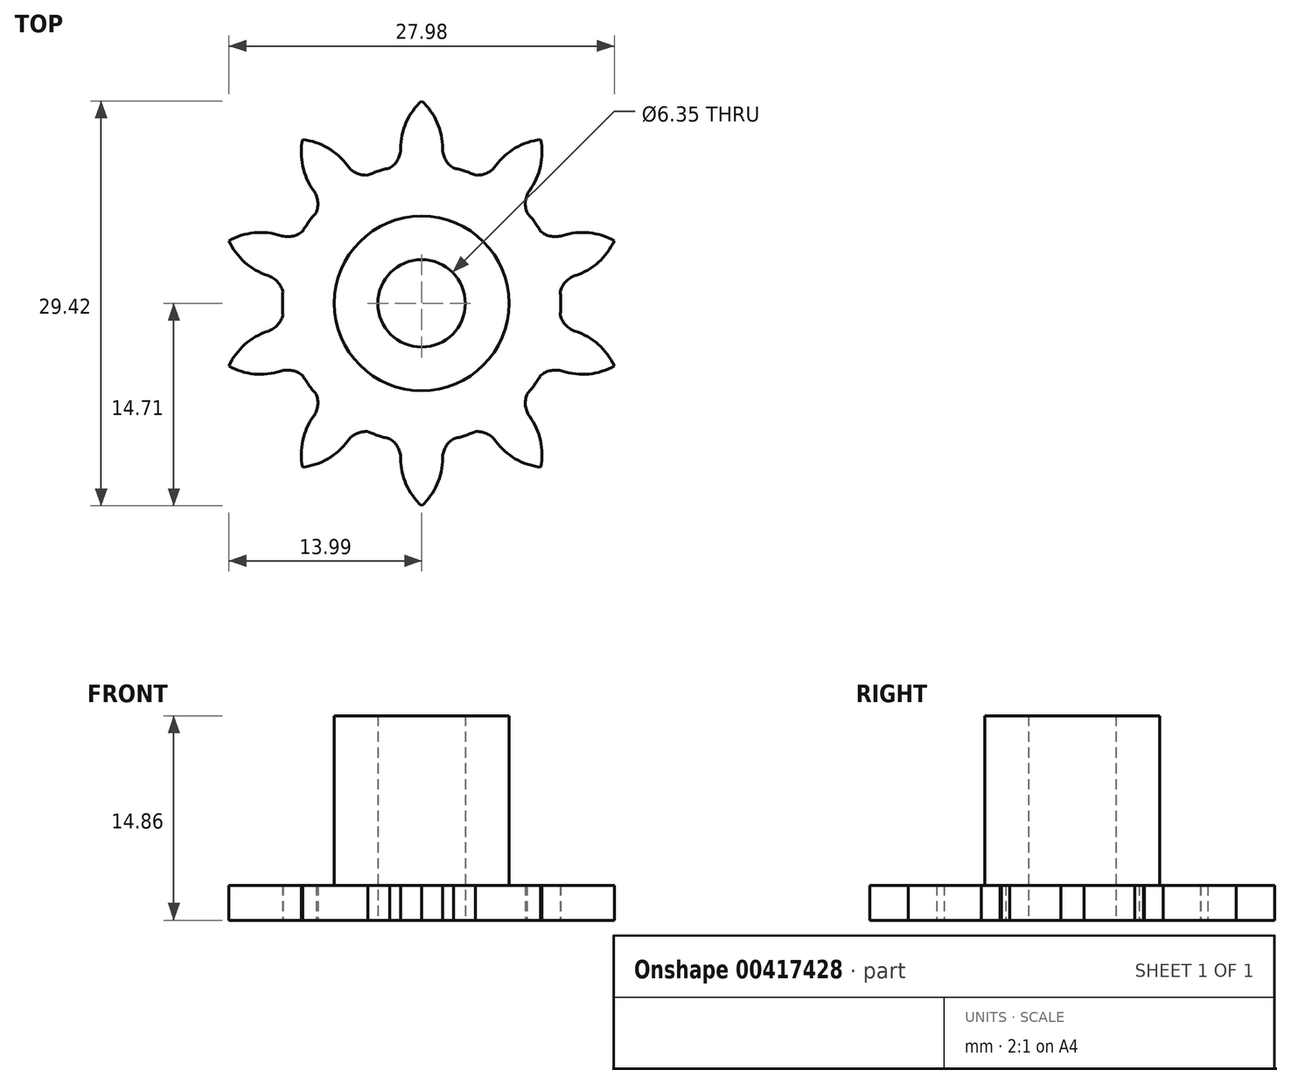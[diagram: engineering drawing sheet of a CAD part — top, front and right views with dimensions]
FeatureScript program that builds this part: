
annotation { "Feature Type Name" : "Feature", "Feature Type Description" : "" }
export const myFeature = defineFeature(function(context is Context, id is Id, definition is map)
    precondition{}
    {
        {
            var Q0;
            Q0=qCreatedBy(makeId("Top.planeOp"),FACE);
            var sketch = newSketch(context, id + "F0", { "sketchPlane" : qUnion([Q0])});
            skCircle(sketch, "E0", {"center": v(0, 0) * mm, "radius": 10.1 * mm});
            skArc(sketch, "E1", {"start": v(-3.18, 9.6) * mm, "mid": v(-2, 10.08) * mm, "end": v(-1.52, 11.25) * mm});
            skArc(sketch, "E2", {"start": v(1.52, 11.25) * mm, "mid": v(2, 10.08) * mm, "end": v(3.18, 9.6) * mm});
            skArc(sketch, "E3", {"start": v(0, 14.71) * mm, "mid": v(-1.13, 13.14) * mm, "end": v(-1.52, 11.25) * mm});
            skArc(sketch, "E4", {"start": v(1.22, 9.6) * mm, "mid": v(1.3, 9.8) * mm, "end": v(1.36, 10.02) * mm});
            skPoint(sketch, "E5", {"position": v(3.18, 9.6) * mm});
            skPoint(sketch, "E6", {"position": v(-3.18, 9.6) * mm});
            skLineSegment(sketch, "E7", {"start": v(-3.18, 9.6) * mm, "end": v(3.18, 9.6) * mm});
            skArc(sketch, "E8.trimOffspring", {"start": v(1.52, 11.25) * mm, "mid": v(1.13, 13.14) * mm, "end": v(0, 14.71) * mm});
            skArc(sketch, "E9.trimOffspring", {"start": v(-1.36, 10.02) * mm, "mid": v(-1.3, 9.8) * mm, "end": v(-1.22, 9.6) * mm});
            skArc(sketch, "E10.1.0", {"start": v(-5.38, 10) * mm, "mid": v(-6.81, 11.3) * mm, "end": v(-8.65, 11.9) * mm});
            skLineSegment(sketch, "E10.1.1", {"start": v(-8.2, 5.9) * mm, "end": v(-3.07, 9.63) * mm});
            skArc(sketch, "E10.1.2", {"start": v(-8.2, 5.9) * mm, "mid": v(-7.55, 6.98) * mm, "end": v(-7.84, 8.2) * mm});
            skArc(sketch, "E10.1.3", {"start": v(-8.65, 11.9) * mm, "mid": v(-8.63, 9.97) * mm, "end": v(-7.84, 8.2) * mm});
            skPoint(sketch, "E10.1.4", {"position": v(-3.07, 9.63) * mm});
            skArc(sketch, "E10.1.5", {"start": v(-5.38, 10) * mm, "mid": v(-4.3, 9.34) * mm, "end": v(-3.07, 9.63) * mm});
            skPoint(sketch, "E10.1.6", {"position": v(-8.2, 5.9) * mm});
            skArc(sketch, "E10.1.7", {"start": v(-6.99, 7.3) * mm, "mid": v(-6.81, 7.17) * mm, "end": v(-6.63, 7.04) * mm});
            skArc(sketch, "E10.1.8", {"start": v(-4.65, 8.48) * mm, "mid": v(-4.71, 8.7) * mm, "end": v(-4.79, 8.9) * mm});
            skArc(sketch, "E10.2.0", {"start": v(-10.23, 4.93) * mm, "mid": v(-12.15, 5.13) * mm, "end": v(-14, 4.55) * mm});
            skLineSegment(sketch, "E10.2.1", {"start": v(-10.1, -0.05) * mm, "end": v(-8.15, 5.99) * mm});
            skArc(sketch, "E10.2.2", {"start": v(-10.1, -0.05) * mm, "mid": v(-10.2, 1.2) * mm, "end": v(-11.17, 2.03) * mm});
            skArc(sketch, "E10.2.3", {"start": v(-14, 4.55) * mm, "mid": v(-12.84, 2.99) * mm, "end": v(-11.17, 2.03) * mm});
            skPoint(sketch, "E10.2.4", {"position": v(-8.15, 5.99) * mm});
            skArc(sketch, "E10.2.5", {"start": v(-10.23, 4.93) * mm, "mid": v(-8.97, 5.02) * mm, "end": v(-8.15, 5.99) * mm});
            skPoint(sketch, "E10.2.6", {"position": v(-10.1, -0.05) * mm});
            skArc(sketch, "E10.2.7", {"start": v(-9.95, 1.8) * mm, "mid": v(-9.73, 1.8) * mm, "end": v(-9.5, 1.8) * mm});
            skArc(sketch, "E10.2.8", {"start": v(-8.75, 4.13) * mm, "mid": v(-8.92, 4.26) * mm, "end": v(-9.1, 4.39) * mm});
            skArc(sketch, "E10.3.0", {"start": v(-11.17, -2.03) * mm, "mid": v(-12.84, -2.99) * mm, "end": v(-14, -4.55) * mm});
            skLineSegment(sketch, "E10.3.1", {"start": v(-8.15, -5.99) * mm, "end": v(-10.1, 0.05) * mm});
            skArc(sketch, "E10.3.2", {"start": v(-8.15, -5.99) * mm, "mid": v(-8.97, -5.02) * mm, "end": v(-10.23, -4.93) * mm});
            skArc(sketch, "E10.3.3", {"start": v(-14, -4.55) * mm, "mid": v(-12.15, -5.13) * mm, "end": v(-10.23, -4.93) * mm});
            skPoint(sketch, "E10.3.4", {"position": v(-10.1, 0.05) * mm});
            skArc(sketch, "E10.3.5", {"start": v(-11.17, -2.03) * mm, "mid": v(-10.2, -1.2) * mm, "end": v(-10.1, 0.05) * mm});
            skPoint(sketch, "E10.3.6", {"position": v(-8.15, -5.99) * mm});
            skArc(sketch, "E10.3.7", {"start": v(-9.1, -4.39) * mm, "mid": v(-8.92, -4.26) * mm, "end": v(-8.75, -4.13) * mm});
            skArc(sketch, "E10.3.8", {"start": v(-9.5, -1.8) * mm, "mid": v(-9.73, -1.8) * mm, "end": v(-9.95, -1.8) * mm});
            skArc(sketch, "E10.4.0", {"start": v(-7.84, -8.2) * mm, "mid": v(-8.63, -9.97) * mm, "end": v(-8.65, -11.9) * mm});
            skLineSegment(sketch, "E10.4.1", {"start": v(-3.07, -9.63) * mm, "end": v(-8.2, -5.9) * mm});
            skArc(sketch, "E10.4.2", {"start": v(-3.07, -9.63) * mm, "mid": v(-4.3, -9.34) * mm, "end": v(-5.38, -10) * mm});
            skArc(sketch, "E10.4.3", {"start": v(-8.65, -11.9) * mm, "mid": v(-6.81, -11.3) * mm, "end": v(-5.38, -10) * mm});
            skPoint(sketch, "E10.4.4", {"position": v(-8.2, -5.9) * mm});
            skArc(sketch, "E10.4.5", {"start": v(-7.84, -8.2) * mm, "mid": v(-7.55, -6.98) * mm, "end": v(-8.2, -5.9) * mm});
            skPoint(sketch, "E10.4.6", {"position": v(-3.07, -9.63) * mm});
            skArc(sketch, "E10.4.7", {"start": v(-4.79, -8.9) * mm, "mid": v(-4.71, -8.7) * mm, "end": v(-4.65, -8.48) * mm});
            skArc(sketch, "E10.4.8", {"start": v(-6.63, -7.04) * mm, "mid": v(-6.81, -7.17) * mm, "end": v(-6.99, -7.3) * mm});
            skArc(sketch, "E10.5.0", {"start": v(-1.52, -11.25) * mm, "mid": v(-1.13, -13.14) * mm, "end": v(0, -14.71) * mm});
            skLineSegment(sketch, "E10.5.1", {"start": v(3.17, -9.6) * mm, "end": v(-3.18, -9.6) * mm});
            skArc(sketch, "E10.5.2", {"start": v(3.17, -9.6) * mm, "mid": v(2, -10.08) * mm, "end": v(1.52, -11.25) * mm});
            skArc(sketch, "E10.5.3", {"start": v(0, -14.71) * mm, "mid": v(1.13, -13.14) * mm, "end": v(1.52, -11.25) * mm});
            skPoint(sketch, "E10.5.4", {"position": v(-3.18, -9.6) * mm});
            skArc(sketch, "E10.5.5", {"start": v(-1.52, -11.25) * mm, "mid": v(-2, -10.08) * mm, "end": v(-3.18, -9.6) * mm});
            skPoint(sketch, "E10.5.6", {"position": v(3.17, -9.6) * mm});
            skArc(sketch, "E10.5.7", {"start": v(1.36, -10.02) * mm, "mid": v(1.3, -9.8) * mm, "end": v(1.22, -9.6) * mm});
            skArc(sketch, "E10.5.8", {"start": v(-1.22, -9.6) * mm, "mid": v(-1.3, -9.8) * mm, "end": v(-1.36, -10.02) * mm});
            skArc(sketch, "E10.6.0", {"start": v(5.38, -10) * mm, "mid": v(6.81, -11.3) * mm, "end": v(8.65, -11.9) * mm});
            skLineSegment(sketch, "E10.6.1", {"start": v(8.2, -5.9) * mm, "end": v(3.07, -9.63) * mm});
            skArc(sketch, "E10.6.2", {"start": v(8.2, -5.9) * mm, "mid": v(7.55, -6.98) * mm, "end": v(7.84, -8.2) * mm});
            skArc(sketch, "E10.6.3", {"start": v(8.65, -11.9) * mm, "mid": v(8.63, -9.97) * mm, "end": v(7.84, -8.2) * mm});
            skPoint(sketch, "E10.6.4", {"position": v(3.07, -9.63) * mm});
            skArc(sketch, "E10.6.5", {"start": v(5.38, -10) * mm, "mid": v(4.3, -9.34) * mm, "end": v(3.07, -9.63) * mm});
            skPoint(sketch, "E10.6.6", {"position": v(8.2, -5.9) * mm});
            skArc(sketch, "E10.6.7", {"start": v(6.99, -7.3) * mm, "mid": v(6.81, -7.17) * mm, "end": v(6.63, -7.04) * mm});
            skArc(sketch, "E10.6.8", {"start": v(4.65, -8.48) * mm, "mid": v(4.71, -8.7) * mm, "end": v(4.79, -8.9) * mm});
            skArc(sketch, "E10.7.0", {"start": v(10.23, -4.93) * mm, "mid": v(12.15, -5.13) * mm, "end": v(14, -4.55) * mm});
            skLineSegment(sketch, "E10.7.1", {"start": v(10.1, 0.05) * mm, "end": v(8.15, -5.99) * mm});
            skArc(sketch, "E10.7.2", {"start": v(10.1, 0.05) * mm, "mid": v(10.2, -1.2) * mm, "end": v(11.17, -2.03) * mm});
            skArc(sketch, "E10.7.3", {"start": v(14, -4.55) * mm, "mid": v(12.84, -2.99) * mm, "end": v(11.17, -2.03) * mm});
            skPoint(sketch, "E10.7.4", {"position": v(8.15, -5.99) * mm});
            skArc(sketch, "E10.7.5", {"start": v(10.23, -4.93) * mm, "mid": v(8.97, -5.02) * mm, "end": v(8.15, -5.99) * mm});
            skPoint(sketch, "E10.7.6", {"position": v(10.1, 0.05) * mm});
            skArc(sketch, "E10.7.7", {"start": v(9.95, -1.8) * mm, "mid": v(9.73, -1.8) * mm, "end": v(9.5, -1.8) * mm});
            skArc(sketch, "E10.7.8", {"start": v(8.75, -4.13) * mm, "mid": v(8.92, -4.26) * mm, "end": v(9.1, -4.39) * mm});
            skArc(sketch, "E10.8.0", {"start": v(11.17, 2.03) * mm, "mid": v(12.84, 2.99) * mm, "end": v(14, 4.55) * mm});
            skLineSegment(sketch, "E10.8.1", {"start": v(8.15, 5.99) * mm, "end": v(10.1, -0.05) * mm});
            skArc(sketch, "E10.8.2", {"start": v(8.15, 5.99) * mm, "mid": v(8.97, 5.02) * mm, "end": v(10.23, 4.93) * mm});
            skArc(sketch, "E10.8.3", {"start": v(14, 4.55) * mm, "mid": v(12.15, 5.13) * mm, "end": v(10.23, 4.93) * mm});
            skPoint(sketch, "E10.8.4", {"position": v(10.1, -0.05) * mm});
            skArc(sketch, "E10.8.5", {"start": v(11.17, 2.03) * mm, "mid": v(10.2, 1.2) * mm, "end": v(10.1, -0.05) * mm});
            skPoint(sketch, "E10.8.6", {"position": v(8.15, 5.99) * mm});
            skArc(sketch, "E10.8.7", {"start": v(9.1, 4.39) * mm, "mid": v(8.92, 4.26) * mm, "end": v(8.75, 4.13) * mm});
            skArc(sketch, "E10.8.8", {"start": v(9.5, 1.8) * mm, "mid": v(9.73, 1.8) * mm, "end": v(9.95, 1.8) * mm});
            skArc(sketch, "E10.9.0", {"start": v(7.84, 8.2) * mm, "mid": v(8.63, 9.97) * mm, "end": v(8.65, 11.9) * mm});
            skLineSegment(sketch, "E10.9.1", {"start": v(3.07, 9.63) * mm, "end": v(8.2, 5.9) * mm});
            skArc(sketch, "E10.9.2", {"start": v(3.07, 9.63) * mm, "mid": v(4.3, 9.34) * mm, "end": v(5.38, 10) * mm});
            skArc(sketch, "E10.9.3", {"start": v(8.65, 11.9) * mm, "mid": v(6.81, 11.3) * mm, "end": v(5.38, 10) * mm});
            skPoint(sketch, "E10.9.4", {"position": v(8.2, 5.9) * mm});
            skArc(sketch, "E10.9.5", {"start": v(7.84, 8.2) * mm, "mid": v(7.55, 6.98) * mm, "end": v(8.2, 5.9) * mm});
            skPoint(sketch, "E10.9.6", {"position": v(3.07, 9.63) * mm});
            skArc(sketch, "E10.9.7", {"start": v(4.79, 8.9) * mm, "mid": v(4.71, 8.7) * mm, "end": v(4.65, 8.48) * mm});
            skArc(sketch, "E10.9.8", {"start": v(6.63, 7.04) * mm, "mid": v(6.81, 7.17) * mm, "end": v(6.99, 7.3) * mm});
            skCircle(sketch, "E11", {"center": v(0, 0) * mm, "radius": 6.35 * mm});
            skCircle(sketch, "E12", {"center": v(0, 0) * mm, "radius": 3.18 * mm});
            skSolve(sketch);
        }
        {
            var Q0;
            {var subQ5=sQuery(id+"F0.wireOp",EDGE,"E10.2.8");Q0=makeQuery(id+"F0.imprint","IMPRINT",FACE,{"disambiguationData":[TD([[makeQuery(id+"F0.imprint","IMPRINT",EDGE,{"derivedFrom":subQ5}),-1.0]])]});}
            var Q1;
            {var subQ0=sQuery(id+"F0.wireOp",EDGE,"E10.3.7");Q1=makeQuery(id+"F0.imprint","IMPRINT",FACE,{"disambiguationData":[TD([[makeQuery(id+"F0.imprint","IMPRINT",EDGE,{"derivedFrom":subQ0}),-1.0]])]});}
            var Q2;
            {var subQ0=sQuery(id+"F0.wireOp",EDGE,"E10.2.7");Q2=makeQuery(id+"F0.imprint","IMPRINT",FACE,{"disambiguationData":[TD([[makeQuery(id+"F0.imprint","IMPRINT",EDGE,{"derivedFrom":subQ0}),-1.0]])]});}
            var Q3;
            {var subQ0=sQuery(id+"F0.wireOp",EDGE,"E10.8.7");Q3=makeQuery(id+"F0.imprint","IMPRINT",FACE,{"disambiguationData":[TD([[makeQuery(id+"F0.imprint","IMPRINT",EDGE,{"derivedFrom":subQ0}),1.0]])]});}
            var Q4;
            {var subQ5=sQuery(id+"F0.wireOp",EDGE,"E10.4.8");Q4=makeQuery(id+"F0.imprint","IMPRINT",FACE,{"disambiguationData":[TD([[makeQuery(id+"F0.imprint","IMPRINT",EDGE,{"derivedFrom":subQ5}),-1.0]])]});}
            var Q5;
            {var subQ0=sQuery(id+"F0.wireOp",EDGE,"E10.3.8");Q5=makeQuery(id+"F0.imprint","IMPRINT",FACE,{"disambiguationData":[TD([[makeQuery(id+"F0.imprint","IMPRINT",EDGE,{"derivedFrom":subQ0}),-1.0]])]});}
            var Q6;
            {var subQ0=sQuery(id+"F0.wireOp",EDGE,"E4");Q6=makeQuery(id+"F0.imprint","IMPRINT",FACE,{"disambiguationData":[TD([[makeQuery(id+"F0.imprint","IMPRINT",EDGE,{"derivedFrom":subQ0}),1.0]])]});}
            var Q7;
            {var subQ4=sQuery(id+"F0.wireOp",EDGE,"E10.8.0");Q7=makeQuery(id+"F0.imprint","IMPRINT",FACE,{"disambiguationData":[TD([[makeQuery(id+"F0.imprint","IMPRINT",EDGE,{"derivedFrom":subQ4}),1.0]])]});}
            var Q8;
            {var subQ5=sQuery(id+"F0.wireOp",EDGE,"E10.5.8");Q8=makeQuery(id+"F0.imprint","IMPRINT",FACE,{"disambiguationData":[TD([[makeQuery(id+"F0.imprint","IMPRINT",EDGE,{"derivedFrom":subQ5}),-1.0]])]});}
            var Q9;
            {var subQ0=sQuery(id+"F0.wireOp",EDGE,"E10.1.7");Q9=makeQuery(id+"F0.imprint","IMPRINT",FACE,{"disambiguationData":[TD([[makeQuery(id+"F0.imprint","IMPRINT",EDGE,{"derivedFrom":subQ0}),1.0]])]});}
            var Q10;
            {var subQ0=sQuery(id+"F0.wireOp",EDGE,"E10.9.0");Q10=makeQuery(id+"F0.imprint","IMPRINT",FACE,{"disambiguationData":[TD([[makeQuery(id+"F0.imprint","IMPRINT",EDGE,{"derivedFrom":subQ0}),1.0]])]});}
            var Q11;
            {var subQ0=sQuery(id+"F0.wireOp",EDGE,"E10.5.7");Q11=makeQuery(id+"F0.imprint","IMPRINT",FACE,{"disambiguationData":[TD([[makeQuery(id+"F0.imprint","IMPRINT",EDGE,{"derivedFrom":subQ0}),-1.0]])]});}
            var Q12;
            {var subQ0=sQuery(id+"F0.wireOp",EDGE,"E10.2.7");Q12=makeQuery(id+"F0.imprint","IMPRINT",FACE,{"disambiguationData":[TD([[makeQuery(id+"F0.imprint","IMPRINT",EDGE,{"derivedFrom":subQ0}),1.0]])]});}
            var Q13;
            {var subQ0=sQuery(id+"F0.wireOp",EDGE,"E10.8.8");Q13=makeQuery(id+"F0.imprint","IMPRINT",FACE,{"disambiguationData":[TD([[makeQuery(id+"F0.imprint","IMPRINT",EDGE,{"derivedFrom":subQ0}),-1.0]])]});}
            var Q14;
            {var subQ5=sQuery(id+"F0.wireOp",EDGE,"E3");Q14=makeQuery(id+"F0.imprint","IMPRINT",FACE,{"disambiguationData":[TD([[makeQuery(id+"F0.imprint","IMPRINT",EDGE,{"derivedFrom":subQ5}),1.0]])]});}
            var Q15;
            {var subQ7=sQuery(id+"F0.wireOp",EDGE,"E10.6.8");Q15=makeQuery(id+"F0.imprint","IMPRINT",FACE,{"disambiguationData":[TD([[makeQuery(id+"F0.imprint","IMPRINT",EDGE,{"derivedFrom":subQ7}),-1.0]])]});}
            var Q16;
            {var subQ0=sQuery(id+"F0.wireOp",EDGE,"E10.8.7");Q16=makeQuery(id+"F0.imprint","IMPRINT",FACE,{"disambiguationData":[TD([[makeQuery(id+"F0.imprint","IMPRINT",EDGE,{"derivedFrom":subQ0}),-1.0]])]});}
            var Q17;
            {var subQ0=sQuery(id+"F0.wireOp",EDGE,"E10.3.7");Q17=makeQuery(id+"F0.imprint","IMPRINT",FACE,{"disambiguationData":[TD([[makeQuery(id+"F0.imprint","IMPRINT",EDGE,{"derivedFrom":subQ0}),1.0]])]});}
            var Q18;
            {var subQ5=sQuery(id+"F0.wireOp",EDGE,"E10.1.0");Q18=makeQuery(id+"F0.imprint","IMPRINT",FACE,{"disambiguationData":[TD([[makeQuery(id+"F0.imprint","IMPRINT",EDGE,{"derivedFrom":subQ5}),1.0]])]});}
            var Q19;
            {var subQ5=sQuery(id+"F0.wireOp",EDGE,"E10.6.7");Q19=makeQuery(id+"F0.imprint","IMPRINT",FACE,{"disambiguationData":[TD([[makeQuery(id+"F0.imprint","IMPRINT",EDGE,{"derivedFrom":subQ5}),-1.0]])]});}
            var Q20;
            {var subQ5=sQuery(id+"F0.wireOp",EDGE,"E10.9.8");Q20=makeQuery(id+"F0.imprint","IMPRINT",FACE,{"disambiguationData":[TD([[makeQuery(id+"F0.imprint","IMPRINT",EDGE,{"derivedFrom":subQ5}),-1.0]])]});}
            var Q21;
            {var subQ0=sQuery(id+"F0.wireOp",EDGE,"E10.4.7");Q21=makeQuery(id+"F0.imprint","IMPRINT",FACE,{"disambiguationData":[TD([[makeQuery(id+"F0.imprint","IMPRINT",EDGE,{"derivedFrom":subQ0}),1.0]])]});}
            var Q22;
            {var subQ0=sQuery(id+"F0.wireOp",EDGE,"E10.2.0");Q22=makeQuery(id+"F0.imprint","IMPRINT",FACE,{"disambiguationData":[TD([[makeQuery(id+"F0.imprint","IMPRINT",EDGE,{"derivedFrom":subQ0}),1.0]])]});}
            var Q23;
            {var subQ5=sQuery(id+"F0.wireOp",EDGE,"E10.7.8");Q23=makeQuery(id+"F0.imprint","IMPRINT",FACE,{"disambiguationData":[TD([[makeQuery(id+"F0.imprint","IMPRINT",EDGE,{"derivedFrom":subQ5}),-1.0]])]});}
            var Q24;
            {var subQ7=sQuery(id+"F0.wireOp",EDGE,"E10.9.7");Q24=makeQuery(id+"F0.imprint","IMPRINT",FACE,{"disambiguationData":[TD([[makeQuery(id+"F0.imprint","IMPRINT",EDGE,{"derivedFrom":subQ7}),-1.0]])]});}
            var Q25;
            {var subQ0=sQuery(id+"F0.wireOp",EDGE,"E10.5.7");Q25=makeQuery(id+"F0.imprint","IMPRINT",FACE,{"disambiguationData":[TD([[makeQuery(id+"F0.imprint","IMPRINT",EDGE,{"derivedFrom":subQ0}),1.0]])]});}
            var Q26;
            {var subQ4=sQuery(id+"F0.wireOp",EDGE,"E10.3.0");Q26=makeQuery(id+"F0.imprint","IMPRINT",FACE,{"disambiguationData":[TD([[makeQuery(id+"F0.imprint","IMPRINT",EDGE,{"derivedFrom":subQ4}),1.0]])]});}
            var Q27;
            {var subQ0=sQuery(id+"F0.wireOp",EDGE,"E10.7.7");Q27=makeQuery(id+"F0.imprint","IMPRINT",FACE,{"disambiguationData":[TD([[makeQuery(id+"F0.imprint","IMPRINT",EDGE,{"derivedFrom":subQ0}),-1.0]])]});}
            var Q28;
            Q28=makeQuery(id+"F0.imprint","IMPRINT",FACE,{"disambiguationData":[TD([[makeQuery(id+"F0.imprint","IMPRINT",EDGE,{"derivedFrom":sQuery(id+"F0.wireOp",EDGE,"E11")}),-1.0]])]});
            var Q29;
            {var subQ1=sQuery(id+"F0.wireOp",EDGE,"E4");Q29=makeQuery(id+"F0.imprint","IMPRINT",FACE,{"disambiguationData":[TD([[makeQuery(id+"F0.imprint","IMPRINT",EDGE,{"derivedFrom":subQ1}),-1.0]])]});}
            var Q30;
            {var subQ0=sQuery(id+"F0.wireOp",EDGE,"E10.6.7");Q30=makeQuery(id+"F0.imprint","IMPRINT",FACE,{"disambiguationData":[TD([[makeQuery(id+"F0.imprint","IMPRINT",EDGE,{"derivedFrom":subQ0}),1.0]])]});}
            var Q31;
            {var subQ0=sQuery(id+"F0.wireOp",EDGE,"E10.4.0");Q31=makeQuery(id+"F0.imprint","IMPRINT",FACE,{"disambiguationData":[TD([[makeQuery(id+"F0.imprint","IMPRINT",EDGE,{"derivedFrom":subQ0}),1.0]])]});}
            var Q32;
            {var subQ0=sQuery(id+"F0.wireOp",EDGE,"E10.5.0");Q32=makeQuery(id+"F0.imprint","IMPRINT",FACE,{"disambiguationData":[TD([[makeQuery(id+"F0.imprint","IMPRINT",EDGE,{"derivedFrom":subQ0}),1.0]])]});}
            var Q33;
            {var subQ0=sQuery(id+"F0.wireOp",EDGE,"E9.trimOffspring");Q33=makeQuery(id+"F0.imprint","IMPRINT",FACE,{"disambiguationData":[TD([[makeQuery(id+"F0.imprint","IMPRINT",EDGE,{"derivedFrom":subQ0}),-1.0]])]});}
            var Q34;
            {var subQ0=sQuery(id+"F0.wireOp",EDGE,"E10.7.7");Q34=makeQuery(id+"F0.imprint","IMPRINT",FACE,{"disambiguationData":[TD([[makeQuery(id+"F0.imprint","IMPRINT",EDGE,{"derivedFrom":subQ0}),1.0]])]});}
            var Q35;
            {var subQ5=sQuery(id+"F0.wireOp",EDGE,"E10.6.0");Q35=makeQuery(id+"F0.imprint","IMPRINT",FACE,{"disambiguationData":[TD([[makeQuery(id+"F0.imprint","IMPRINT",EDGE,{"derivedFrom":subQ5}),1.0]])]});}
            var Q36;
            {var subQ7=sQuery(id+"F0.wireOp",EDGE,"E10.1.8");Q36=makeQuery(id+"F0.imprint","IMPRINT",FACE,{"disambiguationData":[TD([[makeQuery(id+"F0.imprint","IMPRINT",EDGE,{"derivedFrom":subQ7}),-1.0]])]});}
            var Q37;
            {var subQ0=sQuery(id+"F0.wireOp",EDGE,"E10.7.0");Q37=makeQuery(id+"F0.imprint","IMPRINT",FACE,{"disambiguationData":[TD([[makeQuery(id+"F0.imprint","IMPRINT",EDGE,{"derivedFrom":subQ0}),1.0]])]});}
            var Q38;
            {var subQ0=sQuery(id+"F0.wireOp",EDGE,"E10.4.7");Q38=makeQuery(id+"F0.imprint","IMPRINT",FACE,{"disambiguationData":[TD([[makeQuery(id+"F0.imprint","IMPRINT",EDGE,{"derivedFrom":subQ0}),-1.0]])]});}
            var Q39;
            {var subQ0=sQuery(id+"F0.wireOp",EDGE,"E10.9.7");Q39=makeQuery(id+"F0.imprint","IMPRINT",FACE,{"disambiguationData":[TD([[makeQuery(id+"F0.imprint","IMPRINT",EDGE,{"derivedFrom":subQ0}),1.0]])]});}
            var Q40;
            {var subQ5=sQuery(id+"F0.wireOp",EDGE,"E10.1.7");Q40=makeQuery(id+"F0.imprint","IMPRINT",FACE,{"disambiguationData":[TD([[makeQuery(id+"F0.imprint","IMPRINT",EDGE,{"derivedFrom":subQ5}),-1.0]])]});}
            var Q41;
            {var subQ1=sQuery(id+"F0.wireOp",EDGE,"E0");var subQ3=sQuery(id+"F0.wireOp",EDGE,"E10.6.2");var subQ4=makeQuery(id+"F0.imprint","INTERSECT",VERTEX,{"derivedFrom":[subQ1,subQ3]});Q41=makeQuery(id+"F0.imprint","IMPRINT",FACE,{"disambiguationData":[TD([[makeQuery(id+"F0.imprint","IMPRINT",EDGE,{"disambiguationData":[TD([[subQ4,1.0]])],"derivedFrom":subQ3}),1.0]])]});}
            var Q42;
            {var subQ1=sQuery(id+"F0.wireOp",EDGE,"E0");var subQ3=sQuery(id+"F0.wireOp",EDGE,"E10.7.2");var subQ4=makeQuery(id+"F0.imprint","INTERSECT",VERTEX,{"derivedFrom":[subQ1,subQ3]});Q42=makeQuery(id+"F0.imprint","IMPRINT",FACE,{"disambiguationData":[TD([[makeQuery(id+"F0.imprint","IMPRINT",EDGE,{"disambiguationData":[TD([[subQ4,1.0]])],"derivedFrom":subQ3}),1.0]])]});}
            var Q43;
            {var subQ1=sQuery(id+"F0.wireOp",EDGE,"E0");var subQ3=sQuery(id+"F0.wireOp",EDGE,"E10.7.5");var subQ4=makeQuery(id+"F0.imprint","INTERSECT",VERTEX,{"derivedFrom":[subQ1,subQ3]});Q43=makeQuery(id+"F0.imprint","IMPRINT",FACE,{"disambiguationData":[TD([[makeQuery(id+"F0.imprint","IMPRINT",EDGE,{"disambiguationData":[TD([[subQ4,-1.0]])],"derivedFrom":subQ3}),1.0]])]});}
            var Q44;
            {var subQ1=sQuery(id+"F0.wireOp",EDGE,"E0");var subQ3=sQuery(id+"F0.wireOp",EDGE,"E10.3.5");var subQ4=makeQuery(id+"F0.imprint","INTERSECT",VERTEX,{"derivedFrom":[subQ1,subQ3]});Q44=makeQuery(id+"F0.imprint","IMPRINT",FACE,{"disambiguationData":[TD([[makeQuery(id+"F0.imprint","IMPRINT",EDGE,{"disambiguationData":[TD([[subQ4,-1.0]])],"derivedFrom":subQ3}),1.0]])]});}
            var Q45;
            {var subQ1=sQuery(id+"F0.wireOp",EDGE,"E0");var subQ3=sQuery(id+"F0.wireOp",EDGE,"E10.3.2");var subQ4=makeQuery(id+"F0.imprint","INTERSECT",VERTEX,{"derivedFrom":[subQ1,subQ3]});Q45=makeQuery(id+"F0.imprint","IMPRINT",FACE,{"disambiguationData":[TD([[makeQuery(id+"F0.imprint","IMPRINT",EDGE,{"disambiguationData":[TD([[subQ4,1.0]])],"derivedFrom":subQ3}),1.0]])]});}
            var Q46;
            {var subQ1=sQuery(id+"F0.wireOp",EDGE,"E0");var subQ3=sQuery(id+"F0.wireOp",EDGE,"E10.4.5");var subQ4=makeQuery(id+"F0.imprint","INTERSECT",VERTEX,{"derivedFrom":[subQ1,subQ3]});Q46=makeQuery(id+"F0.imprint","IMPRINT",FACE,{"disambiguationData":[TD([[makeQuery(id+"F0.imprint","IMPRINT",EDGE,{"disambiguationData":[TD([[subQ4,-1.0]])],"derivedFrom":subQ3}),1.0]])]});}
            var Q47;
            {var subQ1=sQuery(id+"F0.wireOp",EDGE,"E0");var subQ3=sQuery(id+"F0.wireOp",EDGE,"E10.4.2");var subQ4=makeQuery(id+"F0.imprint","INTERSECT",VERTEX,{"derivedFrom":[subQ1,subQ3]});Q47=makeQuery(id+"F0.imprint","IMPRINT",FACE,{"disambiguationData":[TD([[makeQuery(id+"F0.imprint","IMPRINT",EDGE,{"disambiguationData":[TD([[subQ4,1.0]])],"derivedFrom":subQ3}),1.0]])]});}
            var Q48;
            {var subQ1=sQuery(id+"F0.wireOp",EDGE,"E0");var subQ3=sQuery(id+"F0.wireOp",EDGE,"E10.5.5");var subQ4=makeQuery(id+"F0.imprint","INTERSECT",VERTEX,{"derivedFrom":[subQ1,subQ3]});Q48=makeQuery(id+"F0.imprint","IMPRINT",FACE,{"disambiguationData":[TD([[makeQuery(id+"F0.imprint","IMPRINT",EDGE,{"disambiguationData":[TD([[subQ4,-1.0]])],"derivedFrom":subQ3}),1.0]])]});}
            var Q49;
            {var subQ1=sQuery(id+"F0.wireOp",EDGE,"E0");var subQ3=sQuery(id+"F0.wireOp",EDGE,"E10.2.5");var subQ4=makeQuery(id+"F0.imprint","INTERSECT",VERTEX,{"derivedFrom":[subQ1,subQ3]});Q49=makeQuery(id+"F0.imprint","IMPRINT",FACE,{"disambiguationData":[TD([[makeQuery(id+"F0.imprint","IMPRINT",EDGE,{"disambiguationData":[TD([[subQ4,-1.0]])],"derivedFrom":subQ3}),1.0]])]});}
            var Q50;
            {var subQ1=sQuery(id+"F0.wireOp",EDGE,"E0");var subQ3=sQuery(id+"F0.wireOp",EDGE,"E10.2.2");var subQ4=makeQuery(id+"F0.imprint","INTERSECT",VERTEX,{"derivedFrom":[subQ1,subQ3]});Q50=makeQuery(id+"F0.imprint","IMPRINT",FACE,{"disambiguationData":[TD([[makeQuery(id+"F0.imprint","IMPRINT",EDGE,{"disambiguationData":[TD([[subQ4,1.0]])],"derivedFrom":subQ3}),1.0]])]});}
            var Q51;
            {var subQ1=sQuery(id+"F0.wireOp",EDGE,"E0");var subQ3=sQuery(id+"F0.wireOp",EDGE,"E10.8.5");var subQ4=makeQuery(id+"F0.imprint","INTERSECT",VERTEX,{"derivedFrom":[subQ1,subQ3]});Q51=makeQuery(id+"F0.imprint","IMPRINT",FACE,{"disambiguationData":[TD([[makeQuery(id+"F0.imprint","IMPRINT",EDGE,{"disambiguationData":[TD([[subQ4,-1.0]])],"derivedFrom":subQ3}),1.0]])]});}
            var Q52;
            {var subQ1=sQuery(id+"F0.wireOp",EDGE,"E0");var subQ3=sQuery(id+"F0.wireOp",EDGE,"E10.8.2");var subQ4=makeQuery(id+"F0.imprint","INTERSECT",VERTEX,{"derivedFrom":[subQ1,subQ3]});Q52=makeQuery(id+"F0.imprint","IMPRINT",FACE,{"disambiguationData":[TD([[makeQuery(id+"F0.imprint","IMPRINT",EDGE,{"disambiguationData":[TD([[subQ4,1.0]])],"derivedFrom":subQ3}),1.0]])]});}
            var Q53;
            {var subQ1=sQuery(id+"F0.wireOp",EDGE,"E0");var subQ3=sQuery(id+"F0.wireOp",EDGE,"E10.9.5");var subQ4=makeQuery(id+"F0.imprint","INTERSECT",VERTEX,{"derivedFrom":[subQ1,subQ3]});Q53=makeQuery(id+"F0.imprint","IMPRINT",FACE,{"disambiguationData":[TD([[makeQuery(id+"F0.imprint","IMPRINT",EDGE,{"disambiguationData":[TD([[subQ4,-1.0]])],"derivedFrom":subQ3}),1.0]])]});}
            var Q54;
            {var subQ1=sQuery(id+"F0.wireOp",EDGE,"E0");var subQ3=sQuery(id+"F0.wireOp",EDGE,"E10.9.2");var subQ4=makeQuery(id+"F0.imprint","INTERSECT",VERTEX,{"derivedFrom":[subQ1,subQ3]});Q54=makeQuery(id+"F0.imprint","IMPRINT",FACE,{"disambiguationData":[TD([[makeQuery(id+"F0.imprint","IMPRINT",EDGE,{"disambiguationData":[TD([[subQ4,1.0]])],"derivedFrom":subQ3}),1.0]])]});}
            var Q55;
            {var subQ1=sQuery(id+"F0.wireOp",EDGE,"E0");var subQ3=sQuery(id+"F0.wireOp",EDGE,"E2");var subQ4=makeQuery(id+"F0.imprint","INTERSECT",VERTEX,{"derivedFrom":[subQ1,subQ3]});Q55=makeQuery(id+"F0.imprint","IMPRINT",FACE,{"disambiguationData":[TD([[makeQuery(id+"F0.imprint","IMPRINT",EDGE,{"disambiguationData":[TD([[subQ4,-1.0]])],"derivedFrom":subQ3}),1.0]])]});}
            var Q56;
            {var subQ1=sQuery(id+"F0.wireOp",EDGE,"E0");var subQ3=sQuery(id+"F0.wireOp",EDGE,"E1");var subQ4=makeQuery(id+"F0.imprint","INTERSECT",VERTEX,{"derivedFrom":[subQ1,subQ3]});Q56=makeQuery(id+"F0.imprint","IMPRINT",FACE,{"disambiguationData":[TD([[makeQuery(id+"F0.imprint","IMPRINT",EDGE,{"disambiguationData":[TD([[subQ4,1.0]])],"derivedFrom":subQ3}),1.0]])]});}
            var Q57;
            {var subQ1=sQuery(id+"F0.wireOp",EDGE,"E0");var subQ3=sQuery(id+"F0.wireOp",EDGE,"E10.1.5");var subQ4=makeQuery(id+"F0.imprint","INTERSECT",VERTEX,{"derivedFrom":[subQ1,subQ3]});Q57=makeQuery(id+"F0.imprint","IMPRINT",FACE,{"disambiguationData":[TD([[makeQuery(id+"F0.imprint","IMPRINT",EDGE,{"disambiguationData":[TD([[subQ4,-1.0]])],"derivedFrom":subQ3}),1.0]])]});}
            var Q58;
            {var subQ1=sQuery(id+"F0.wireOp",EDGE,"E0");var subQ3=sQuery(id+"F0.wireOp",EDGE,"E10.1.2");var subQ4=makeQuery(id+"F0.imprint","INTERSECT",VERTEX,{"derivedFrom":[subQ1,subQ3]});Q58=makeQuery(id+"F0.imprint","IMPRINT",FACE,{"disambiguationData":[TD([[makeQuery(id+"F0.imprint","IMPRINT",EDGE,{"disambiguationData":[TD([[subQ4,1.0]])],"derivedFrom":subQ3}),1.0]])]});}
            var Q59;
            {var subQ1=sQuery(id+"F0.wireOp",EDGE,"E0");var subQ3=sQuery(id+"F0.wireOp",EDGE,"E10.5.2");var subQ4=makeQuery(id+"F0.imprint","INTERSECT",VERTEX,{"derivedFrom":[subQ1,subQ3]});Q59=makeQuery(id+"F0.imprint","IMPRINT",FACE,{"disambiguationData":[TD([[makeQuery(id+"F0.imprint","IMPRINT",EDGE,{"disambiguationData":[TD([[subQ4,1.0]])],"derivedFrom":subQ3}),1.0]])]});}
            var Q60;
            {var subQ1=sQuery(id+"F0.wireOp",EDGE,"E0");var subQ3=sQuery(id+"F0.wireOp",EDGE,"E10.6.5");var subQ4=makeQuery(id+"F0.imprint","INTERSECT",VERTEX,{"derivedFrom":[subQ1,subQ3]});Q60=makeQuery(id+"F0.imprint","IMPRINT",FACE,{"disambiguationData":[TD([[makeQuery(id+"F0.imprint","IMPRINT",EDGE,{"disambiguationData":[TD([[subQ4,-1.0]])],"derivedFrom":subQ3}),1.0]])]});}
            var Q61;
            {var subQ1=sQuery(id+"F0.wireOp",EDGE,"E10.7.1");var subQ3=sQuery(id+"F0.wireOp",EDGE,"E10.8.5");var subQ4=makeQuery(id+"F0.imprint","INTERSECT",VERTEX,{"derivedFrom":[subQ1,subQ3]});Q61=makeQuery(id+"F0.imprint","IMPRINT",FACE,{"disambiguationData":[TD([[makeQuery(id+"F0.imprint","IMPRINT",EDGE,{"disambiguationData":[TD([[subQ4,-1.0]])],"derivedFrom":subQ3}),1.0]])]});}
            var Q62;
            {var subQ1=sQuery(id+"F0.wireOp",EDGE,"E1");var subQ3=sQuery(id+"F0.wireOp",EDGE,"E10.1.5");var subQ4=makeQuery(id+"F0.imprint","INTERSECT",VERTEX,{"derivedFrom":[subQ1,subQ3]});Q62=makeQuery(id+"F0.imprint","IMPRINT",FACE,{"disambiguationData":[TD([[makeQuery(id+"F0.imprint","IMPRINT",EDGE,{"disambiguationData":[TD([[subQ4,1.0]])],"derivedFrom":subQ3}),1.0]])]});}
            var Q63;
            {var subQ0=sQuery(id+"F0.wireOp",EDGE,"E10.2.5");var subQ1=sQuery(id+"F0.wireOp",EDGE,"E10.1.1");var subQ2=makeQuery(id+"F0.imprint","INTERSECT",VERTEX,{"derivedFrom":[subQ1,subQ0]});Q63=makeQuery(id+"F0.imprint","IMPRINT",FACE,{"disambiguationData":[TD([[makeQuery(id+"F0.imprint","IMPRINT",EDGE,{"disambiguationData":[TD([[subQ2,-1.0]])],"derivedFrom":subQ1}),1.0]])]});}
            var Q64;
            {var subQ0=sQuery(id+"F0.wireOp",EDGE,"E10.5.5");var subQ1=sQuery(id+"F0.wireOp",EDGE,"E10.4.1");var subQ2=makeQuery(id+"F0.imprint","INTERSECT",VERTEX,{"derivedFrom":[subQ1,subQ0]});Q64=makeQuery(id+"F0.imprint","IMPRINT",FACE,{"disambiguationData":[TD([[makeQuery(id+"F0.imprint","IMPRINT",EDGE,{"disambiguationData":[TD([[subQ2,-1.0]])],"derivedFrom":subQ1}),1.0]])]});}
            var Q65;
            {var subQ0=sQuery(id+"F0.wireOp",EDGE,"E10.9.5");var subQ1=sQuery(id+"F0.wireOp",EDGE,"E10.8.2");var subQ2=makeQuery(id+"F0.imprint","INTERSECT",VERTEX,{"derivedFrom":[subQ1,subQ0]});Q65=makeQuery(id+"F0.imprint","IMPRINT",FACE,{"disambiguationData":[TD([[makeQuery(id+"F0.imprint","IMPRINT",EDGE,{"disambiguationData":[TD([[subQ2,-1.0]])],"derivedFrom":subQ1}),1.0]])]});}
            var Q66;
            {var subQ0=sQuery(id+"F0.wireOp",EDGE,"E10.8.5");var subQ1=sQuery(id+"F0.wireOp",EDGE,"E10.7.2");var subQ2=makeQuery(id+"F0.imprint","INTERSECT",VERTEX,{"derivedFrom":[subQ1,subQ0]});Q66=makeQuery(id+"F0.imprint","IMPRINT",FACE,{"disambiguationData":[TD([[makeQuery(id+"F0.imprint","IMPRINT",EDGE,{"disambiguationData":[TD([[subQ2,-1.0]])],"derivedFrom":subQ1}),1.0]])]});}
            var Q67;
            {var subQ1=sQuery(id+"F0.wireOp",EDGE,"E2");var subQ3=sQuery(id+"F0.wireOp",EDGE,"E10.9.2");var subQ4=makeQuery(id+"F0.imprint","INTERSECT",VERTEX,{"derivedFrom":[subQ1,subQ3]});Q67=makeQuery(id+"F0.imprint","IMPRINT",FACE,{"disambiguationData":[TD([[makeQuery(id+"F0.imprint","IMPRINT",EDGE,{"disambiguationData":[TD([[subQ4,-1.0]])],"derivedFrom":subQ3}),1.0]])]});}
            var Q68;
            {var subQ0=sQuery(id+"F0.wireOp",EDGE,"E10.1.5");var subQ1=sQuery(id+"F0.wireOp",EDGE,"E1");var subQ2=makeQuery(id+"F0.imprint","INTERSECT",VERTEX,{"derivedFrom":[subQ1,subQ0]});Q68=makeQuery(id+"F0.imprint","IMPRINT",FACE,{"disambiguationData":[TD([[makeQuery(id+"F0.imprint","IMPRINT",EDGE,{"disambiguationData":[TD([[subQ2,-1.0]])],"derivedFrom":subQ1}),1.0]])]});}
            var Q69;
            {var subQ0=sQuery(id+"F0.wireOp",EDGE,"E10.6.2");var subQ3=sQuery(id+"F0.wireOp",EDGE,"E10.7.5");var subQ5=makeQuery(id+"F0.imprint","INTERSECT",VERTEX,{"derivedFrom":[subQ0,subQ3]});Q69=makeQuery(id+"F0.imprint","IMPRINT",FACE,{"disambiguationData":[TD([[makeQuery(id+"F0.imprint","IMPRINT",EDGE,{"disambiguationData":[TD([[subQ5,1.0]])],"derivedFrom":subQ0}),1.0]])]});}
            var Q70;
            {var subQ0=sQuery(id+"F0.wireOp",EDGE,"E10.3.5");var subQ1=sQuery(id+"F0.wireOp",EDGE,"E10.2.1");var subQ2=makeQuery(id+"F0.imprint","INTERSECT",VERTEX,{"derivedFrom":[subQ1,subQ0]});Q70=makeQuery(id+"F0.imprint","IMPRINT",FACE,{"disambiguationData":[TD([[makeQuery(id+"F0.imprint","IMPRINT",EDGE,{"disambiguationData":[TD([[subQ2,-1.0]])],"derivedFrom":subQ1}),1.0]])]});}
            var Q71;
            {var subQ0=sQuery(id+"F0.wireOp",EDGE,"E10.6.5");var subQ1=sQuery(id+"F0.wireOp",EDGE,"E10.5.1");var subQ2=makeQuery(id+"F0.imprint","INTERSECT",VERTEX,{"derivedFrom":[subQ1,subQ0]});Q71=makeQuery(id+"F0.imprint","IMPRINT",FACE,{"disambiguationData":[TD([[makeQuery(id+"F0.imprint","IMPRINT",EDGE,{"disambiguationData":[TD([[subQ2,-1.0]])],"derivedFrom":subQ1}),1.0]])]});}
            var Q72;
            {var subQ1=sQuery(id+"F0.wireOp",EDGE,"E10.1.1");var subQ3=sQuery(id+"F0.wireOp",EDGE,"E10.2.5");var subQ4=makeQuery(id+"F0.imprint","INTERSECT",VERTEX,{"derivedFrom":[subQ1,subQ3]});Q72=makeQuery(id+"F0.imprint","IMPRINT",FACE,{"disambiguationData":[TD([[makeQuery(id+"F0.imprint","IMPRINT",EDGE,{"disambiguationData":[TD([[subQ4,-1.0]])],"derivedFrom":subQ3}),1.0]])]});}
            var Q73;
            {var subQ0=sQuery(id+"F0.wireOp",EDGE,"E10.9.1");var subQ1=sQuery(id+"F0.wireOp",EDGE,"E2");var subQ2=makeQuery(id+"F0.imprint","INTERSECT",VERTEX,{"derivedFrom":[subQ1,subQ0]});Q73=makeQuery(id+"F0.imprint","IMPRINT",FACE,{"disambiguationData":[TD([[makeQuery(id+"F0.imprint","IMPRINT",EDGE,{"disambiguationData":[TD([[subQ2,-1.0]])],"derivedFrom":subQ1}),1.0]])]});}
            var Q74;
            {var subQ0=sQuery(id+"F0.wireOp",EDGE,"E10.4.5");var subQ1=sQuery(id+"F0.wireOp",EDGE,"E10.3.1");var subQ2=makeQuery(id+"F0.imprint","INTERSECT",VERTEX,{"derivedFrom":[subQ1,subQ0]});Q74=makeQuery(id+"F0.imprint","IMPRINT",FACE,{"disambiguationData":[TD([[makeQuery(id+"F0.imprint","IMPRINT",EDGE,{"disambiguationData":[TD([[subQ2,-1.0]])],"derivedFrom":subQ1}),1.0]])]});}
            var Q75;
            {var subQ1=sQuery(id+"F0.wireOp",EDGE,"E10.2.1");var subQ3=sQuery(id+"F0.wireOp",EDGE,"E10.3.5");var subQ4=makeQuery(id+"F0.imprint","INTERSECT",VERTEX,{"derivedFrom":[subQ1,subQ3]});Q75=makeQuery(id+"F0.imprint","IMPRINT",FACE,{"disambiguationData":[TD([[makeQuery(id+"F0.imprint","IMPRINT",EDGE,{"disambiguationData":[TD([[subQ4,-1.0]])],"derivedFrom":subQ3}),1.0]])]});}
            var Q76;
            {var subQ0=sQuery(id+"F0.wireOp",EDGE,"E10.3.5");var subQ1=sQuery(id+"F0.wireOp",EDGE,"E10.2.2");var subQ2=makeQuery(id+"F0.imprint","INTERSECT",VERTEX,{"derivedFrom":[subQ1,subQ0]});Q76=makeQuery(id+"F0.imprint","IMPRINT",FACE,{"disambiguationData":[TD([[makeQuery(id+"F0.imprint","IMPRINT",EDGE,{"disambiguationData":[TD([[subQ2,-1.0]])],"derivedFrom":subQ1}),1.0]])]});}
            var Q77;
            {var subQ0=sQuery(id+"F0.wireOp",EDGE,"E10.3.2");var subQ3=sQuery(id+"F0.wireOp",EDGE,"E10.4.5");var subQ5=makeQuery(id+"F0.imprint","INTERSECT",VERTEX,{"derivedFrom":[subQ0,subQ3]});Q77=makeQuery(id+"F0.imprint","IMPRINT",FACE,{"disambiguationData":[TD([[makeQuery(id+"F0.imprint","IMPRINT",EDGE,{"disambiguationData":[TD([[subQ5,1.0]])],"derivedFrom":subQ0}),1.0]])]});}
            var Q78;
            {var subQ1=sQuery(id+"F0.wireOp",EDGE,"E10.4.1");var subQ3=sQuery(id+"F0.wireOp",EDGE,"E10.5.5");var subQ4=makeQuery(id+"F0.imprint","INTERSECT",VERTEX,{"derivedFrom":[subQ1,subQ3]});Q78=makeQuery(id+"F0.imprint","IMPRINT",FACE,{"disambiguationData":[TD([[makeQuery(id+"F0.imprint","IMPRINT",EDGE,{"disambiguationData":[TD([[subQ4,-1.0]])],"derivedFrom":subQ3}),1.0]])]});}
            var Q79;
            {var subQ0=sQuery(id+"F0.wireOp",EDGE,"E10.4.2");var subQ3=sQuery(id+"F0.wireOp",EDGE,"E10.5.5");var subQ5=makeQuery(id+"F0.imprint","INTERSECT",VERTEX,{"derivedFrom":[subQ0,subQ3]});Q79=makeQuery(id+"F0.imprint","IMPRINT",FACE,{"disambiguationData":[TD([[makeQuery(id+"F0.imprint","IMPRINT",EDGE,{"disambiguationData":[TD([[subQ5,1.0]])],"derivedFrom":subQ0}),1.0]])]});}
            var Q80;
            {var subQ0=sQuery(id+"F0.wireOp",EDGE,"E10.6.5");var subQ1=sQuery(id+"F0.wireOp",EDGE,"E10.5.2");var subQ2=makeQuery(id+"F0.imprint","INTERSECT",VERTEX,{"derivedFrom":[subQ1,subQ0]});Q80=makeQuery(id+"F0.imprint","IMPRINT",FACE,{"disambiguationData":[TD([[makeQuery(id+"F0.imprint","IMPRINT",EDGE,{"disambiguationData":[TD([[subQ2,-1.0]])],"derivedFrom":subQ1}),1.0]])]});}
            var Q81;
            {var subQ0=sQuery(id+"F0.wireOp",EDGE,"E10.7.2");var subQ3=sQuery(id+"F0.wireOp",EDGE,"E10.8.5");var subQ5=makeQuery(id+"F0.imprint","INTERSECT",VERTEX,{"derivedFrom":[subQ0,subQ3]});Q81=makeQuery(id+"F0.imprint","IMPRINT",FACE,{"disambiguationData":[TD([[makeQuery(id+"F0.imprint","IMPRINT",EDGE,{"disambiguationData":[TD([[subQ5,1.0]])],"derivedFrom":subQ0}),1.0]])]});}
            var Q82;
            {var subQ1=sQuery(id+"F0.wireOp",EDGE,"E10.8.1");var subQ3=sQuery(id+"F0.wireOp",EDGE,"E10.9.5");var subQ4=makeQuery(id+"F0.imprint","INTERSECT",VERTEX,{"derivedFrom":[subQ1,subQ3]});Q82=makeQuery(id+"F0.imprint","IMPRINT",FACE,{"disambiguationData":[TD([[makeQuery(id+"F0.imprint","IMPRINT",EDGE,{"disambiguationData":[TD([[subQ4,-1.0]])],"derivedFrom":subQ3}),1.0]])]});}
            var Q83;
            {var subQ1=sQuery(id+"F0.wireOp",EDGE,"E10.3.1");var subQ3=sQuery(id+"F0.wireOp",EDGE,"E10.4.5");var subQ4=makeQuery(id+"F0.imprint","INTERSECT",VERTEX,{"derivedFrom":[subQ1,subQ3]});Q83=makeQuery(id+"F0.imprint","IMPRINT",FACE,{"disambiguationData":[TD([[makeQuery(id+"F0.imprint","IMPRINT",EDGE,{"disambiguationData":[TD([[subQ4,-1.0]])],"derivedFrom":subQ3}),1.0]])]});}
            var Q84;
            {var subQ0=sQuery(id+"F0.wireOp",EDGE,"E10.4.5");var subQ1=sQuery(id+"F0.wireOp",EDGE,"E10.3.2");var subQ2=makeQuery(id+"F0.imprint","INTERSECT",VERTEX,{"derivedFrom":[subQ1,subQ0]});Q84=makeQuery(id+"F0.imprint","IMPRINT",FACE,{"disambiguationData":[TD([[makeQuery(id+"F0.imprint","IMPRINT",EDGE,{"disambiguationData":[TD([[subQ2,-1.0]])],"derivedFrom":subQ1}),1.0]])]});}
            var Q85;
            {var subQ0=sQuery(id+"F0.wireOp",EDGE,"E10.5.5");var subQ1=sQuery(id+"F0.wireOp",EDGE,"E10.4.2");var subQ2=makeQuery(id+"F0.imprint","INTERSECT",VERTEX,{"derivedFrom":[subQ1,subQ0]});Q85=makeQuery(id+"F0.imprint","IMPRINT",FACE,{"disambiguationData":[TD([[makeQuery(id+"F0.imprint","IMPRINT",EDGE,{"disambiguationData":[TD([[subQ2,-1.0]])],"derivedFrom":subQ1}),1.0]])]});}
            var Q86;
            {var subQ1=sQuery(id+"F0.wireOp",EDGE,"E10.5.1");var subQ3=sQuery(id+"F0.wireOp",EDGE,"E10.6.5");var subQ4=makeQuery(id+"F0.imprint","INTERSECT",VERTEX,{"derivedFrom":[subQ1,subQ3]});Q86=makeQuery(id+"F0.imprint","IMPRINT",FACE,{"disambiguationData":[TD([[makeQuery(id+"F0.imprint","IMPRINT",EDGE,{"disambiguationData":[TD([[subQ4,-1.0]])],"derivedFrom":subQ3}),1.0]])]});}
            var Q87;
            {var subQ0=sQuery(id+"F0.wireOp",EDGE,"E10.2.2");var subQ3=sQuery(id+"F0.wireOp",EDGE,"E10.3.5");var subQ5=makeQuery(id+"F0.imprint","INTERSECT",VERTEX,{"derivedFrom":[subQ0,subQ3]});Q87=makeQuery(id+"F0.imprint","IMPRINT",FACE,{"disambiguationData":[TD([[makeQuery(id+"F0.imprint","IMPRINT",EDGE,{"disambiguationData":[TD([[subQ5,1.0]])],"derivedFrom":subQ0}),1.0]])]});}
            var Q88;
            {var subQ0=sQuery(id+"F0.wireOp",EDGE,"E10.8.2");var subQ3=sQuery(id+"F0.wireOp",EDGE,"E10.9.5");var subQ5=makeQuery(id+"F0.imprint","INTERSECT",VERTEX,{"derivedFrom":[subQ0,subQ3]});Q88=makeQuery(id+"F0.imprint","IMPRINT",FACE,{"disambiguationData":[TD([[makeQuery(id+"F0.imprint","IMPRINT",EDGE,{"disambiguationData":[TD([[subQ5,1.0]])],"derivedFrom":subQ0}),1.0]])]});}
            var Q89;
            {var subQ0=sQuery(id+"F0.wireOp",EDGE,"E2");var subQ3=sQuery(id+"F0.wireOp",EDGE,"E10.9.2");var subQ5=makeQuery(id+"F0.imprint","INTERSECT",VERTEX,{"derivedFrom":[subQ0,subQ3]});Q89=makeQuery(id+"F0.imprint","IMPRINT",FACE,{"disambiguationData":[TD([[makeQuery(id+"F0.imprint","IMPRINT",EDGE,{"disambiguationData":[TD([[subQ5,-1.0]])],"derivedFrom":subQ0}),1.0]])]});}
            var Q90;
            {var subQ0=sQuery(id+"F0.wireOp",EDGE,"E1");var subQ3=sQuery(id+"F0.wireOp",EDGE,"E10.1.5");var subQ5=makeQuery(id+"F0.imprint","INTERSECT",VERTEX,{"derivedFrom":[subQ0,subQ3]});Q90=makeQuery(id+"F0.imprint","IMPRINT",FACE,{"disambiguationData":[TD([[makeQuery(id+"F0.imprint","IMPRINT",EDGE,{"disambiguationData":[TD([[subQ5,1.0]])],"derivedFrom":subQ0}),1.0]])]});}
            var Q91;
            {var subQ0=sQuery(id+"F0.wireOp",EDGE,"E10.1.2");var subQ3=sQuery(id+"F0.wireOp",EDGE,"E10.2.5");var subQ5=makeQuery(id+"F0.imprint","INTERSECT",VERTEX,{"derivedFrom":[subQ0,subQ3]});Q91=makeQuery(id+"F0.imprint","IMPRINT",FACE,{"disambiguationData":[TD([[makeQuery(id+"F0.imprint","IMPRINT",EDGE,{"disambiguationData":[TD([[subQ5,1.0]])],"derivedFrom":subQ0}),1.0]])]});}
            var Q92;
            {var subQ1=sQuery(id+"F0.wireOp",EDGE,"E10.6.1");var subQ3=sQuery(id+"F0.wireOp",EDGE,"E10.7.5");var subQ4=makeQuery(id+"F0.imprint","INTERSECT",VERTEX,{"derivedFrom":[subQ1,subQ3]});Q92=makeQuery(id+"F0.imprint","IMPRINT",FACE,{"disambiguationData":[TD([[makeQuery(id+"F0.imprint","IMPRINT",EDGE,{"disambiguationData":[TD([[subQ4,-1.0]])],"derivedFrom":subQ3}),1.0]])]});}
            var Q93;
            {var subQ0=sQuery(id+"F0.wireOp",EDGE,"E10.5.2");var subQ3=sQuery(id+"F0.wireOp",EDGE,"E10.6.5");var subQ5=makeQuery(id+"F0.imprint","INTERSECT",VERTEX,{"derivedFrom":[subQ0,subQ3]});Q93=makeQuery(id+"F0.imprint","IMPRINT",FACE,{"disambiguationData":[TD([[makeQuery(id+"F0.imprint","IMPRINT",EDGE,{"disambiguationData":[TD([[subQ5,1.0]])],"derivedFrom":subQ0}),1.0]])]});}
            var Q94;
            {var subQ0=sQuery(id+"F0.wireOp",EDGE,"E10.8.5");var subQ1=sQuery(id+"F0.wireOp",EDGE,"E10.7.1");var subQ2=makeQuery(id+"F0.imprint","INTERSECT",VERTEX,{"derivedFrom":[subQ1,subQ0]});Q94=makeQuery(id+"F0.imprint","IMPRINT",FACE,{"disambiguationData":[TD([[makeQuery(id+"F0.imprint","IMPRINT",EDGE,{"disambiguationData":[TD([[subQ2,-1.0]])],"derivedFrom":subQ1}),1.0]])]});}
            var Q95;
            {var subQ0=sQuery(id+"F0.wireOp",EDGE,"E10.9.5");var subQ1=sQuery(id+"F0.wireOp",EDGE,"E10.8.1");var subQ2=makeQuery(id+"F0.imprint","INTERSECT",VERTEX,{"derivedFrom":[subQ1,subQ0]});Q95=makeQuery(id+"F0.imprint","IMPRINT",FACE,{"disambiguationData":[TD([[makeQuery(id+"F0.imprint","IMPRINT",EDGE,{"disambiguationData":[TD([[subQ2,-1.0]])],"derivedFrom":subQ1}),1.0]])]});}
            var Q96;
            {var subQ0=sQuery(id+"F0.wireOp",EDGE,"E10.1.5");var subQ1=sQuery(id+"F0.wireOp",EDGE,"E1");var subQ2=makeQuery(id+"F0.imprint","INTERSECT",VERTEX,{"derivedFrom":[subQ1,subQ0]});Q96=makeQuery(id+"F0.imprint","IMPRINT",FACE,{"disambiguationData":[TD([[makeQuery(id+"F0.imprint","IMPRINT",EDGE,{"disambiguationData":[TD([[subQ2,-1.0]])],"derivedFrom":subQ1}),-1.0]])]});}
            var Q97;
            {var subQ0=sQuery(id+"F0.wireOp",EDGE,"E10.7.5");var subQ1=sQuery(id+"F0.wireOp",EDGE,"E10.6.2");var subQ2=makeQuery(id+"F0.imprint","INTERSECT",VERTEX,{"derivedFrom":[subQ1,subQ0]});Q97=makeQuery(id+"F0.imprint","IMPRINT",FACE,{"disambiguationData":[TD([[makeQuery(id+"F0.imprint","IMPRINT",EDGE,{"disambiguationData":[TD([[subQ2,-1.0]])],"derivedFrom":subQ1}),1.0]])]});}
            var Q98;
            {var subQ0=sQuery(id+"F0.wireOp",EDGE,"E10.2.5");var subQ1=sQuery(id+"F0.wireOp",EDGE,"E10.1.2");var subQ2=makeQuery(id+"F0.imprint","INTERSECT",VERTEX,{"derivedFrom":[subQ1,subQ0]});Q98=makeQuery(id+"F0.imprint","IMPRINT",FACE,{"disambiguationData":[TD([[makeQuery(id+"F0.imprint","IMPRINT",EDGE,{"disambiguationData":[TD([[subQ2,-1.0]])],"derivedFrom":subQ1}),1.0]])]});}
            var Q99;
            {var subQ0=sQuery(id+"F0.wireOp",EDGE,"E10.9.1");var subQ1=sQuery(id+"F0.wireOp",EDGE,"E2");var subQ2=makeQuery(id+"F0.imprint","INTERSECT",VERTEX,{"derivedFrom":[subQ1,subQ0]});Q99=makeQuery(id+"F0.imprint","IMPRINT",FACE,{"disambiguationData":[TD([[makeQuery(id+"F0.imprint","IMPRINT",EDGE,{"disambiguationData":[TD([[subQ2,-1.0]])],"derivedFrom":subQ1}),-1.0]])]});}
            var Q100;
            {var subQ0=sQuery(id+"F0.wireOp",EDGE,"E10.7.5");var subQ1=sQuery(id+"F0.wireOp",EDGE,"E10.6.1");var subQ2=makeQuery(id+"F0.imprint","INTERSECT",VERTEX,{"derivedFrom":[subQ1,subQ0]});Q100=makeQuery(id+"F0.imprint","IMPRINT",FACE,{"disambiguationData":[TD([[makeQuery(id+"F0.imprint","IMPRINT",EDGE,{"disambiguationData":[TD([[subQ2,-1.0]])],"derivedFrom":subQ1}),1.0]])]});}
            extrude(context, id + "F1", {"entities" : qUnion([Q0, Q1, Q2, Q3, Q4, Q5, Q6, Q7, Q8, Q9, Q10, Q11, Q12, Q13, Q14, Q15, Q16, Q17, Q18, Q19, Q20, Q21, Q22, Q23, Q24, Q25, Q26, Q27, Q28, Q29, Q30, Q31, Q32, Q33, Q34, Q35, Q36, Q37, Q38, Q39, Q40, Q41, Q42, Q43, Q44, Q45, Q46, Q47, Q48, Q49, Q50, Q51, Q52, Q53, Q54, Q55, Q56, Q57, Q58, Q59, Q60, Q61, Q62, Q63, Q64, Q65, Q66, Q67, Q68, Q69, Q70, Q71, Q72, Q73, Q74, Q75, Q76, Q77, Q78, Q79, Q80, Q81, Q82, Q83, Q84, Q85, Q86, Q87, Q88, Q89, Q90, Q91, Q92, Q93, Q94, Q95, Q96, Q97, Q98, Q99, Q100]), "depth" : 2.54 * mm, "offsetDistance" : 25.4 * mm});
        }
        {
            var Q0;
            Q0=makeQuery(id+"F0.imprint","IMPRINT",FACE,{"disambiguationData":[TD([[makeQuery(id+"F0.imprint","IMPRINT",EDGE,{"derivedFrom":sQuery(id+"F0.wireOp",EDGE,"E11")}),1.0]])]});
            extrude(context, id + "F2", {"entities" : qUnion([Q0]), "operationType" : NewBodyOperationType.ADD, "depth" : 14.86 * mm, "offsetDistance" : 25.4 * mm});
        }
    });
